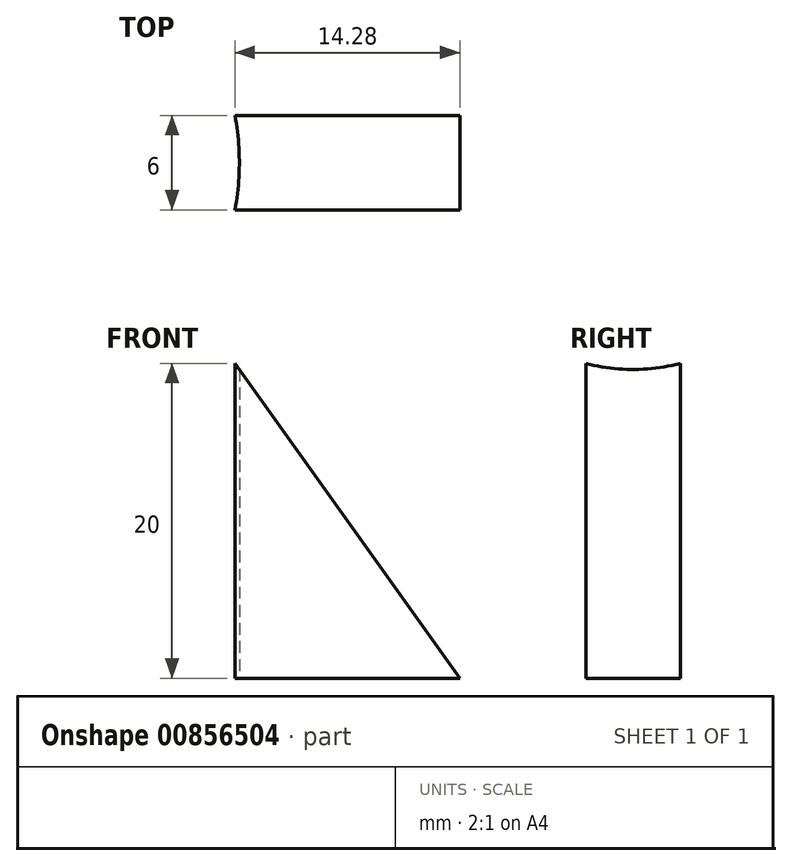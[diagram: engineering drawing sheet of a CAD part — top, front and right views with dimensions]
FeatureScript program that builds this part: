
annotation { "Feature Type Name" : "Feature", "Feature Type Description" : "" }
export const myFeature = defineFeature(function(context is Context, id is Id, definition is map)
    precondition{}
    {
        {
            var Q0;
            Q0=qCreatedBy(makeId("Top.planeOp"),FACE);
            var sketch = newSketch(context, id + "F0", { "sketchPlane" : qUnion([Q0])});
            skLineSegment(sketch, "E0.bottom", {"start": v(-7.14, -3) * mm, "end": v(7.14, -3) * mm});
            skLineSegment(sketch, "E0.top", {"start": v(-7.14, 3) * mm, "end": v(7.14, 3) * mm});
            skLineSegment(sketch, "E0.left", {"start": v(-7.14, -3) * mm, "end": v(-7.14, 3) * mm});
            skLineSegment(sketch, "E0.right", {"start": v(7.14, -3) * mm, "end": v(7.14, 3) * mm});
            skPoint(sketch, "E0.middle", {"position": v(0, 0) * mm});
            skSolve(sketch);
        }
        {
            var Q0;
            Q0=makeQuery(id+"F0.imprint","IMPRINT",FACE,{"disambiguationData":[TD([[makeQuery(id+"F0.imprint","IMPRINT",EDGE,{"derivedFrom":sQuery(id+"F0.wireOp",EDGE,"E0.bottom")}),1.0]])]});
            extrude(context, id + "F1", {"entities" : qUnion([Q0]), "depth" : 20 * mm, "offsetDistance" : 25 * mm});
        }
        {
            var Q0;
            Q0=makeQuery(id+"F1.opExtrude","CAP_EDGE",EDGE,{"disambiguationData":[OSD([sQuery(id+"F0.wireOp",EDGE,"E0.right")])],"isStart":false});
            chamfer(context, id + "F2", {"entities" : qUnion([Q0]), "chamferType" : ChamferType.TWO_OFFSETS, "width1" : 14.28 * mm, "oppositeDirection" : false, "width2" : 20 * mm, "tangentPropagation" : true});
        }
        {
            var Q0;
            Q0=qCreatedBy(makeId("Top.planeOp"),FACE);
            var sketch = newSketch(context, id + "F3", { "sketchPlane" : qUnion([Q0])});
            skPoint(sketch, "E1.0", {"position": v(-7.14, -3) * mm});
            skPoint(sketch, "E2.0", {"position": v(-7.14, 3) * mm});
            skPoint(sketch, "E3", {"position": v(-22.86, 0) * mm});
            skCircle(sketch, "E4", {"center": v(-22.86, 0) * mm, "radius": 16 * mm});
            skSolve(sketch);
        }
        {
            var Q0;
            Q0=makeQuery(id+"F3.imprint","IMPRINT",FACE,{"disambiguationData":[TD([[makeQuery(id+"F3.imprint","IMPRINT",EDGE,{"derivedFrom":sQuery(id+"F3.wireOp",EDGE,"E4")}),1.0]])]});
            extrude(context, id + "F4", {"entities" : qUnion([Q0]), "operationType" : NewBodyOperationType.REMOVE, "depth" : 25 * mm, "offsetDistance" : 25 * mm});
        }
    });
